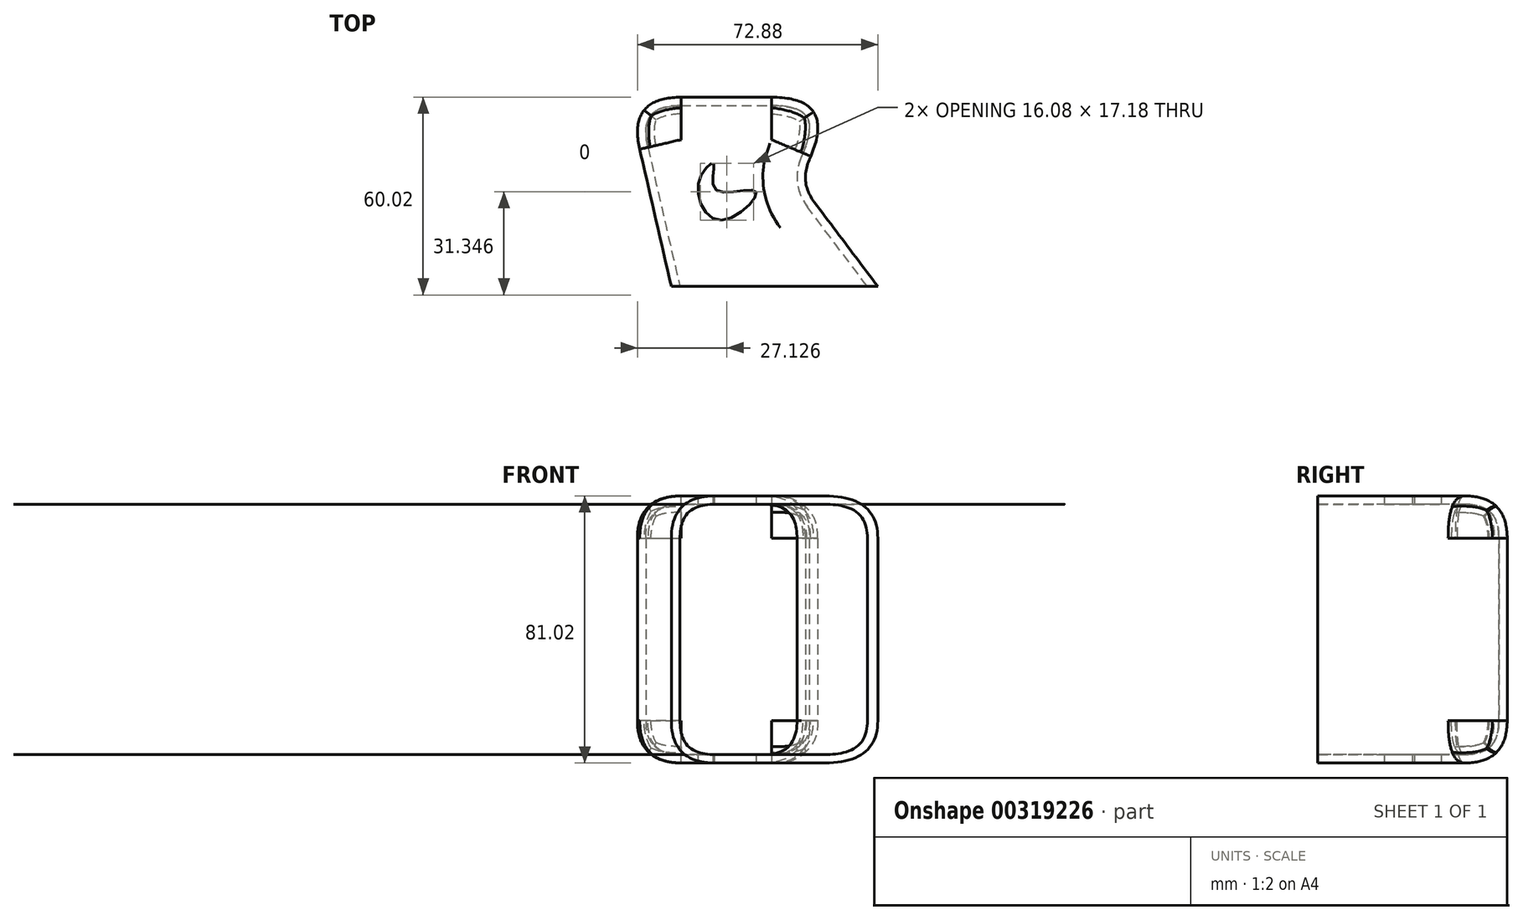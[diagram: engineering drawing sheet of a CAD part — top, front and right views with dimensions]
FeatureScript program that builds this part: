
annotation { "Feature Type Name" : "Feature", "Feature Type Description" : "" }
export const myFeature = defineFeature(function(context is Context, id is Id, definition is map)
    precondition{}
    {
        {
            var Q0;
            Q0=qCreatedBy(makeId("Top.planeOp"),FACE);
            var sketch = newSketch(context, id + "F0", { "sketchPlane" : qUnion([Q0])});
            skLineSegment(sketch, "E0", {"start": v(-38.9, -31.54) * mm, "end": v(-52.1, 25.9) * mm});
            skLineSegment(sketch, "E1", {"start": v(-52.1, 25.9) * mm, "end": v(11.01, 25.9) * mm});
            skLineSegment(sketch, "E2", {"start": v(11.01, 25.9) * mm, "end": v(0, 0) * mm});
            skLineSegment(sketch, "E3", {"start": v(0, 0) * mm, "end": v(23.74, -31.54) * mm});
            skLineSegment(sketch, "E4", {"start": v(23.74, -31.54) * mm, "end": v(-38.9, -31.54) * mm});
            skSolve(sketch);
        }
        {
            var Q0;
            Q0=makeQuery(id+"F0.imprint","IMPRINT",FACE,{"disambiguationData":[TD([[makeQuery(id+"F0.imprint","IMPRINT",EDGE,{"derivedFrom":sQuery(id+"F0.wireOp",EDGE,"E0")}),-1.0]])]});
            extrude(context, id + "F1", {"entities" : qUnion([Q0]), "endBound" : BoundingType.SYMMETRIC, "depth" : 81.03 * mm});
        }
        {
            var Q0;
            Q0=makeQuery(id+"F1.opExtrude","CAP_EDGE",EDGE,{"disambiguationData":[OSD([sQuery(id+"F0.wireOp",EDGE,"E1")])],"isStart":false});
            var Q1;
            Q1=makeQuery(id+"F1.opExtrude","SWEPT_EDGE",EDGE,{"disambiguationData":[OSD([sQuery(id+"F0.wireOp",EDGE,"E1"),sQuery(id+"F0.wireOp",EDGE,"E2")])]});
            var Q2;
            Q2=makeQuery(id+"F1.opExtrude","SWEPT_EDGE",EDGE,{"disambiguationData":[OSD([sQuery(id+"F0.wireOp",EDGE,"E0"),sQuery(id+"F0.wireOp",EDGE,"E1")])]});
            var Q3;
            Q3=makeQuery(id+"F1.opExtrude","CAP_EDGE",EDGE,{"disambiguationData":[OSD([sQuery(id+"F0.wireOp",EDGE,"E1")])],"isStart":true});
            var Q4;
            Q4=makeQuery(id+"F1.opExtrude","CAP_EDGE",EDGE,{"disambiguationData":[OSD([sQuery(id+"F0.wireOp",EDGE,"E2")])],"isStart":false});
            var Q5;
            Q5=makeQuery(id+"F1.opExtrude","CAP_EDGE",EDGE,{"disambiguationData":[OSD([sQuery(id+"F0.wireOp",EDGE,"E0")])],"isStart":false});
            var Q6;
            Q6=makeQuery(id+"F1.opExtrude","CAP_EDGE",EDGE,{"disambiguationData":[OSD([sQuery(id+"F0.wireOp",EDGE,"E0")])],"isStart":true});
            var Q7;
            Q7=makeQuery(id+"F1.opExtrude","SWEPT_EDGE",EDGE,{"disambiguationData":[OSD([sQuery(id+"F0.wireOp",EDGE,"E2"),sQuery(id+"F0.wireOp",EDGE,"E3")])]});
            var Q8;
            Q8=makeQuery(id+"F1.opExtrude","CAP_EDGE",EDGE,{"disambiguationData":[OSD([sQuery(id+"F0.wireOp",EDGE,"E3")])],"isStart":true});
            var Q9;
            Q9=makeQuery(id+"F1.opExtrude","CAP_EDGE",EDGE,{"disambiguationData":[OSD([sQuery(id+"F0.wireOp",EDGE,"E2")])],"isStart":true});
            var Q10;
            Q10=makeQuery(id+"F1.opExtrude","CAP_EDGE",EDGE,{"disambiguationData":[OSD([sQuery(id+"F0.wireOp",EDGE,"E3")])],"isStart":false});
            fillet(context, id + "F2", {"entities" : qUnion([Q0, Q1, Q2, Q3, Q4, Q5, Q6, Q7, Q8, Q9, Q10]), "radius" : 12.88 * mm, "tangentPropagation" : true, "rho" : 0.5, "crossSection" : FilletCrossSection.CONIC, "allowEdgeOverflow" : false});
        }
        {
            var Q0;
            Q0=makeQuery(id+"F1.opExtrude","SWEPT_FACE",FACE,{"disambiguationData":[OSD([sQuery(id+"F0.wireOp",EDGE,"E4")])]});
            shell(context, id + "F3", {"entities" : qUnion([Q0]), "thickness" : 2.54 * mm});
        }
        {
            var Q0;
            Q0=makeQuery(id+"F1.opExtrude","CAP_FACE",FACE,{"disambiguationData":[OSD([sQuery(id+"F0.wireOp",EDGE,"E0"),sQuery(id+"F0.wireOp",EDGE,"E1"),sQuery(id+"F0.wireOp",EDGE,"E2"),sQuery(id+"F0.wireOp",EDGE,"E3"),sQuery(id+"F0.wireOp",EDGE,"E4")])],"isStart":false});
            var sketch = newSketch(context, id + "F4", { "sketchPlane" : qUnion([Q0])});
            skFitSpline(sketch, "E5", {"points": [v(-23.7, -11.36) * mm, v(-30.6, 0) * mm, v(-26.06, 5.66) * mm, v(-25.44, -2.11) * mm, v(-13.29, -2.77) * mm, v(-23.7, -11.36) * mm]});
            skSolve(sketch);
        }
        {
            var Q0;
            {var subQ0=sQuery(id+"F4.wireOp",EDGE,"E5");var subQ1=sQuery(id+"F0.wireOp",EDGE,"E0");var subQ2=makeQuery(id+"F2.opFillet","BLEND_EDGE",EDGE,{"blendedFrom":[makeQuery(id+"F1.opExtrude","CAP_EDGE",EDGE,{"disambiguationData":[OSD([subQ1])],"isStart":false}),makeQuery(id+"F1.opExtrude","CAP_FACE",FACE,{"disambiguationData":[OSD([subQ1,sQuery(id+"F0.wireOp",EDGE,"E1"),sQuery(id+"F0.wireOp",EDGE,"E2"),sQuery(id+"F0.wireOp",EDGE,"E3"),sQuery(id+"F0.wireOp",EDGE,"E4")])],"isStart":false})],"blendedInto":[makeQuery(id+"F1.opExtrude","CAP_FACE",FACE,{"disambiguationData":[OSD([subQ1,sQuery(id+"F0.wireOp",EDGE,"E1"),sQuery(id+"F0.wireOp",EDGE,"E2"),sQuery(id+"F0.wireOp",EDGE,"E3"),sQuery(id+"F0.wireOp",EDGE,"E4")])],"isStart":false})]});var subQ3=makeQuery(id+"F4.imprint","INTERSECT",VERTEX,{"disambiguationData":[OD(0.0)],"derivedFrom":[subQ2,subQ0]});Q0=makeQuery(id+"F4.imprint","IMPRINT",FACE,{"disambiguationData":[TD([[makeQuery(id+"F4.imprint","IMPRINT",EDGE,{"disambiguationData":[TD([[subQ3,-1.0]])],"derivedFrom":subQ0}),-1.0]])]});}
            extrude(context, id + "F5", {"entities" : qUnion([Q0]), "operationType" : NewBodyOperationType.REMOVE, "endBound" : BoundingType.THROUGH_ALL, "oppositeDirection" : true, "depth" : 25.4 * mm});
        }
    });
